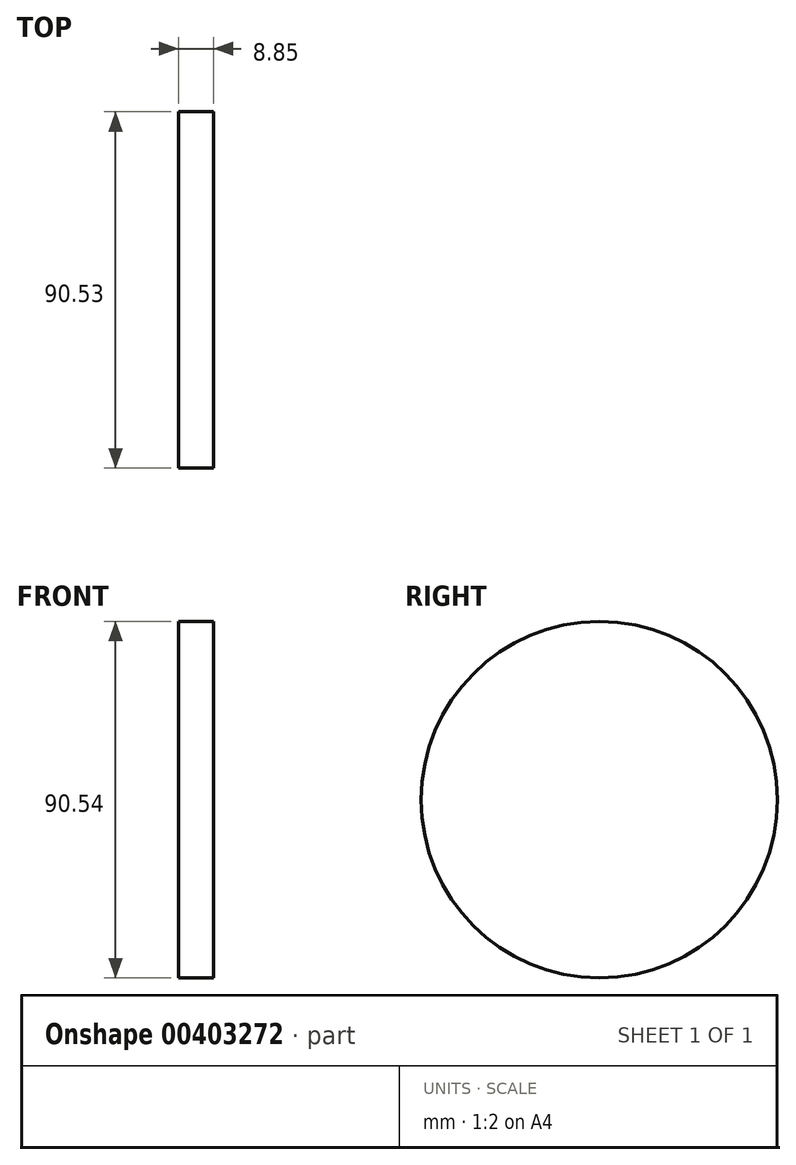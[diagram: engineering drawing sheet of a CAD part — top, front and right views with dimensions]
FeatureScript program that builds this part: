
annotation { "Feature Type Name" : "Feature", "Feature Type Description" : "" }
export const myFeature = defineFeature(function(context is Context, id is Id, definition is map)
    precondition{}
    {
        {
            var Q0;
            Q0=qCreatedBy(makeId("Right.planeOp"),FACE);
            var sketch = newSketch(context, id + "F0", { "sketchPlane" : qUnion([Q0])});
            skCircle(sketch, "E0", {"center": v(-1.34, 0) * mm, "radius": 45.27 * mm});
            skSolve(sketch);
        }
        {
            var Q0;
            Q0 = qSketchRegion(id + "F0", true);
            extrude(context, id + "F1", {"entities" : qUnion([Q0]), "depth" : 8.85 * mm});
        }
    });
